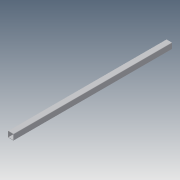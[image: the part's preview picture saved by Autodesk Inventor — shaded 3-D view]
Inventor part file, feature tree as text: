
AUTODESK INVENTOR PART (.ipt)
format: ipt  version: 2014 (Build 180170000, 170)  size: 93,184 bytes
history: native  units: in
note: dims shown in document units (in); Inventor stores cm internally (conversion verified against a paired STEP export)
features: extrude x1, sketch x1
ambient origin geometry x8: Origin, YZ Plane, XZ Plane, XY Plane, X Axis, Y Axis, Z Axis, Center Point
bodies: Solid1 (feature_tree)
feature tree (2):
  extrude  "Extrusion1"  Depth=1.0in
  sketch  "Sketch1"  dims[d0=1.0in d1=1.0in d2=0.07in d3=0.063in d4=27.5in d5=0.0in]
